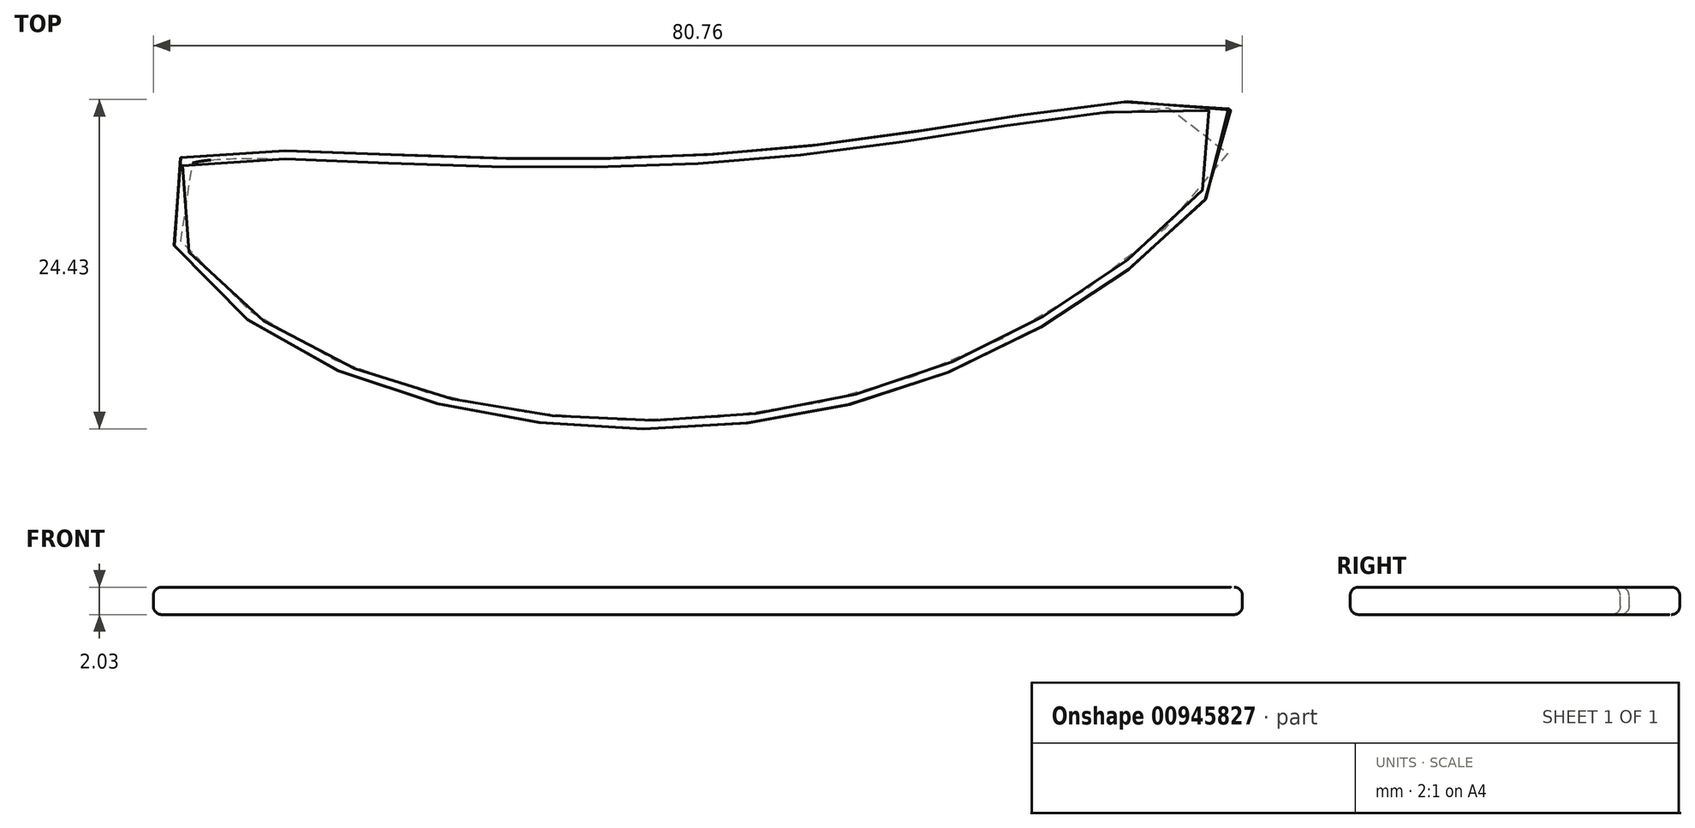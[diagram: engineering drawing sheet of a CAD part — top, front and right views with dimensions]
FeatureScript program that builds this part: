
annotation { "Feature Type Name" : "Feature", "Feature Type Description" : "" }
export const myFeature = defineFeature(function(context is Context, id is Id, definition is map)
    precondition{}
    {
        {
            var Q0;
            Q0=qCreatedBy(makeId("Top.planeOp"),FACE);
            var sketch = newSketch(context, id + "F0", { "sketchPlane" : qUnion([Q0])});
            skFitSpline(sketch, "E0", {"points": [v(-78.18, -23.56) * mm, v(-87.78, -25.51) * mm, v(-79.6, -37.07) * mm, v(-30.17, -40.45) * mm, v(-7.41, -21.25) * mm, v(-39.42, -23.2) * mm, v(-78.18, -23.56) * mm]});
            skSolve(sketch);
        }
        {
            var Q0;
            Q0=makeQuery(id+"F0.imprint","IMPRINT",FACE,{"disambiguationData":[TD([[makeQuery(id+"F0.imprint","IMPRINT",EDGE,{"derivedFrom":sQuery(id+"F0.wireOp",EDGE,"E0")}),1.0]])]});
            extrude(context, id + "F1", {"entities" : qUnion([Q0]), "depth" : 2.03 * mm, "offsetDistance" : 25.4 * mm});
        }
        {
            var Q0;
            Q0=makeQuery(id+"F1.opExtrude","CAP_EDGE",EDGE,{"disambiguationData":[OSD([sQuery(id+"F0.wireOp",EDGE,"E0")])],"isStart":false});
            var Q1;
            Q1=makeQuery(id+"F1.opExtrude","CAP_EDGE",EDGE,{"disambiguationData":[OSD([sQuery(id+"F0.wireOp",EDGE,"E0")])],"isStart":true});
            fillet(context, id + "F2", {"entities" : qUnion([Q0, Q1]), "radius" : 0.61 * mm, "tangentPropagation" : true, "allowEdgeOverflow" : false});
        }
    });
